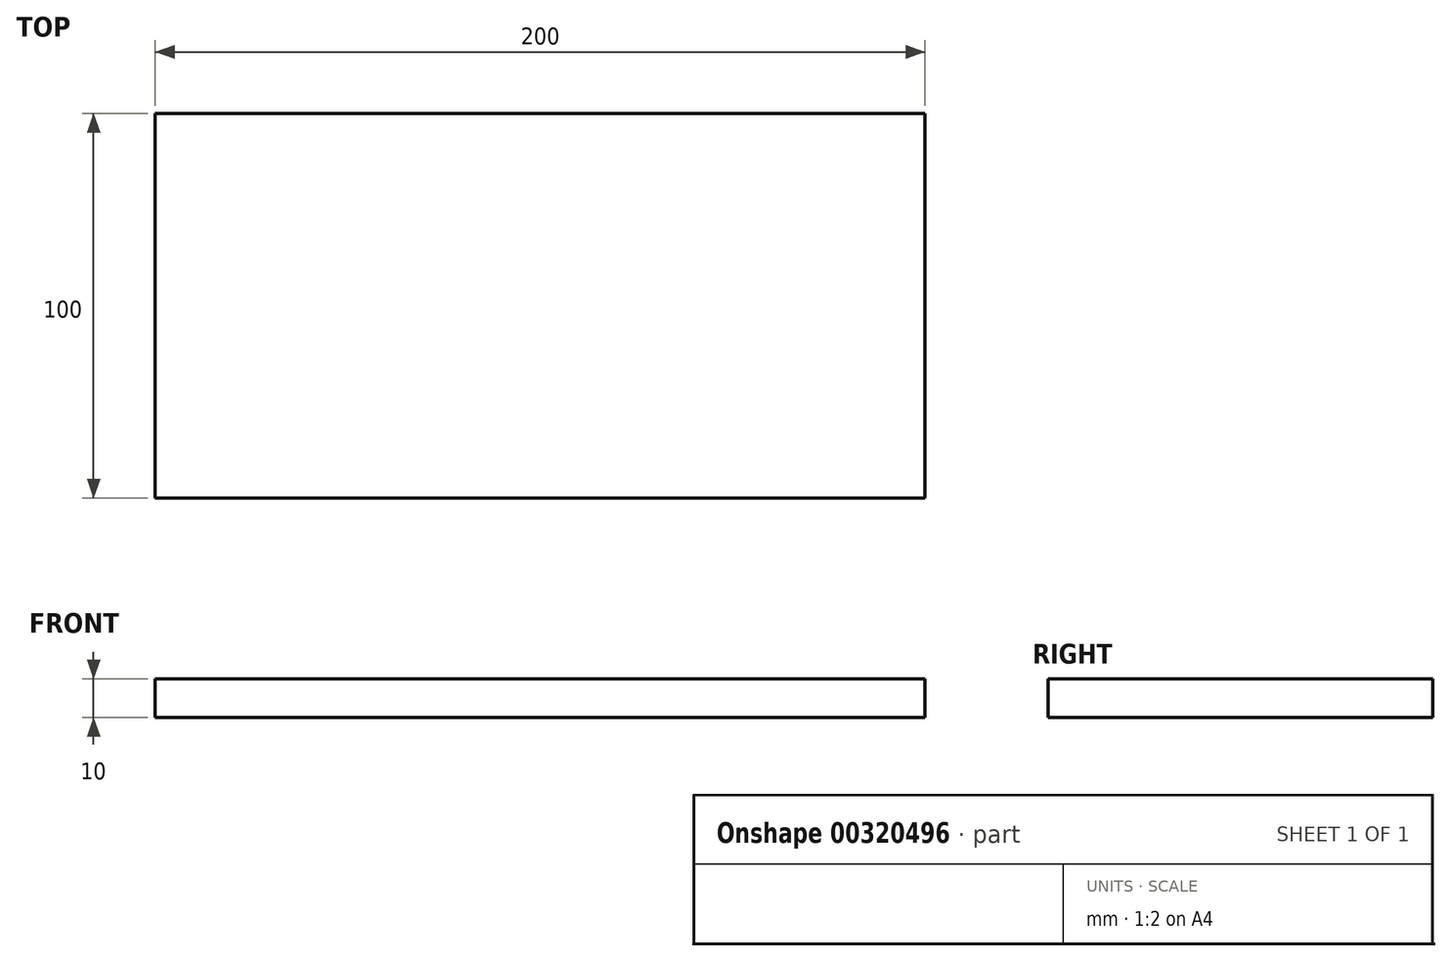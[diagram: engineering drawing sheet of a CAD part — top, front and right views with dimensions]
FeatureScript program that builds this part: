
annotation { "Feature Type Name" : "Feature", "Feature Type Description" : "" }
export const myFeature = defineFeature(function(context is Context, id is Id, definition is map)
    precondition{}
    {
        {
            var Q0;
            Q0=qCreatedBy(makeId("Top.planeOp"),FACE);
            var sketch = newSketch(context, id + "F0", { "sketchPlane" : qUnion([Q0])});
            skLineSegment(sketch, "E0.bottom", {"start": v(100, -50) * mm, "end": v(-100, -50) * mm});
            skLineSegment(sketch, "E0.top", {"start": v(100, 50) * mm, "end": v(-100, 50) * mm});
            skLineSegment(sketch, "E0.left", {"start": v(100, -50) * mm, "end": v(100, 50) * mm});
            skLineSegment(sketch, "E0.right", {"start": v(-100, -50) * mm, "end": v(-100, 50) * mm});
            skPoint(sketch, "E0.middle", {"position": v(0, 0) * mm});
            skSolve(sketch);
        }
        {
            var Q0;
            Q0=makeQuery(id+"F0.imprint","IMPRINT",FACE,{"disambiguationData":[TD([[makeQuery(id+"F0.imprint","IMPRINT",EDGE,{"derivedFrom":sQuery(id+"F0.wireOp",EDGE,"E0.bottom")}),-1.0]])]});
            extrude(context, id + "F1", {"entities" : qUnion([Q0]), "depth" : 10 * mm});
        }
    });
